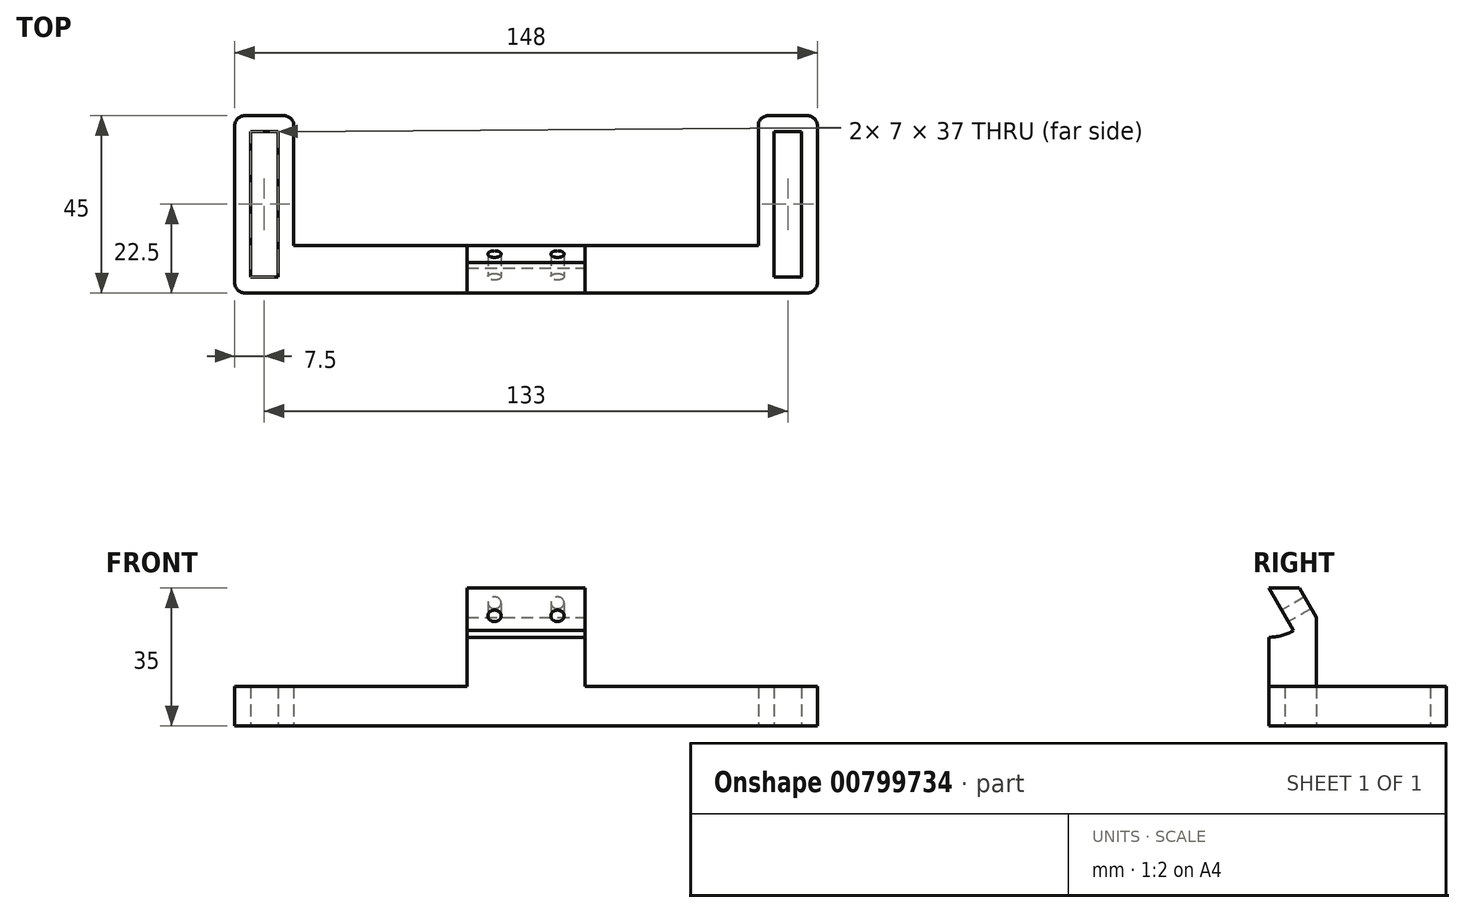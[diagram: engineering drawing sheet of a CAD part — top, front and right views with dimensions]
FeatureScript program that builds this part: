
annotation { "Feature Type Name" : "Feature", "Feature Type Description" : "" }
export const myFeature = defineFeature(function(context is Context, id is Id, definition is map)
    precondition{}
    {
        {
            var Q0;
            Q0=qCreatedBy(makeId("Top.planeOp"),FACE);
            var sketch = newSketch(context, id + "F0", { "sketchPlane" : qUnion([Q0])});
            skPoint(sketch, "E0", {"position": v(59, 0) * mm});
            skPoint(sketch, "E1", {"position": v(-59, 0) * mm});
            skLineSegment(sketch, "E2.bottom", {"start": v(-59, 0) * mm, "end": v(-74, 0) * mm});
            skLineSegment(sketch, "E2.top", {"start": v(-59, 45) * mm, "end": v(-74, 45) * mm});
            skLineSegment(sketch, "E2.left", {"start": v(-59, 0) * mm, "end": v(-59, 45) * mm});
            skLineSegment(sketch, "E2.right", {"start": v(-74, 0) * mm, "end": v(-74, 45) * mm});
            skLineSegment(sketch, "E3.bottom", {"start": v(59, 0) * mm, "end": v(74, 0) * mm});
            skLineSegment(sketch, "E3.top", {"start": v(59, 45) * mm, "end": v(74, 45) * mm});
            skLineSegment(sketch, "E3.left", {"start": v(59, 0) * mm, "end": v(59, 45) * mm});
            skLineSegment(sketch, "E3.right", {"start": v(74, 0) * mm, "end": v(74, 45) * mm});
            skPoint(sketch, "E4", {"position": v(59, 12) * mm});
            skPoint(sketch, "E5", {"position": v(-59, 12) * mm});
            skLineSegment(sketch, "E6", {"start": v(-59, 12) * mm, "end": v(59, 12) * mm});
            skLineSegment(sketch, "E7", {"start": v(-59, 0) * mm, "end": v(59, 0) * mm});
            skLineSegment(sketch, "E8.0", {"start": v(-70, 4) * mm, "end": v(-70, 41) * mm});
            skLineSegment(sketch, "E8.1", {"start": v(-63, 4) * mm, "end": v(-70, 4) * mm});
            skLineSegment(sketch, "E8.2", {"start": v(-63, 4) * mm, "end": v(-63, 41) * mm});
            skLineSegment(sketch, "E8.3", {"start": v(-63, 41) * mm, "end": v(-70, 41) * mm});
            skLineSegment(sketch, "E9.0", {"start": v(70, 4) * mm, "end": v(70, 41) * mm});
            skLineSegment(sketch, "E9.1", {"start": v(63, 4) * mm, "end": v(70, 4) * mm});
            skLineSegment(sketch, "E9.2", {"start": v(63, 4) * mm, "end": v(63, 41) * mm});
            skLineSegment(sketch, "E9.3", {"start": v(63, 41) * mm, "end": v(70, 41) * mm});
            skSolve(sketch);
        }
        {
            var Q0;
            {var subQ2=sQuery(id+"F0.wireOp",EDGE,"E6");Q0=makeQuery(id+"F0.imprint","IMPRINT",FACE,{"disambiguationData":[TD([[makeQuery(id+"F0.imprint","IMPRINT",EDGE,{"derivedFrom":subQ2}),-1.0]])]});}
            var Q1;
            {var subQ1=sQuery(id+"F0.wireOp",EDGE,"E2.bottom");Q1=makeQuery(id+"F0.imprint","IMPRINT",FACE,{"disambiguationData":[TD([[makeQuery(id+"F0.imprint","IMPRINT",EDGE,{"derivedFrom":subQ1}),-1.0]])]});}
            var Q2;
            {var subQ1=sQuery(id+"F0.wireOp",EDGE,"E3.bottom");Q2=makeQuery(id+"F0.imprint","IMPRINT",FACE,{"disambiguationData":[TD([[makeQuery(id+"F0.imprint","IMPRINT",EDGE,{"derivedFrom":subQ1}),1.0]])]});}
            extrude(context, id + "F1", {"entities" : qUnion([Q0, Q1, Q2]), "depth" : 10 * mm, "offsetDistance" : 25 * mm});
        }
        {
            var Q0;
            Q0=makeQuery(id+"F1.opExtrude","CAP_FACE",FACE,{"disambiguationData":[OSD([sQuery(id+"F0.wireOp",EDGE,"E2.bottom"),sQuery(id+"F0.wireOp",EDGE,"E2.top"),sQuery(id+"F0.wireOp",EDGE,"E2.left"),sQuery(id+"F0.wireOp",EDGE,"E2.right"),sQuery(id+"F0.wireOp",EDGE,"E3.bottom"),sQuery(id+"F0.wireOp",EDGE,"E3.top"),sQuery(id+"F0.wireOp",EDGE,"E3.left"),sQuery(id+"F0.wireOp",EDGE,"E3.right"),sQuery(id+"F0.wireOp",EDGE,"E6"),sQuery(id+"F0.wireOp",EDGE,"E7"),sQuery(id+"F0.wireOp",EDGE,"E8.0"),sQuery(id+"F0.wireOp",EDGE,"E8.1"),sQuery(id+"F0.wireOp",EDGE,"E8.2"),sQuery(id+"F0.wireOp",EDGE,"E8.3"),sQuery(id+"F0.wireOp",EDGE,"E9.0"),sQuery(id+"F0.wireOp",EDGE,"E9.1"),sQuery(id+"F0.wireOp",EDGE,"E9.2"),sQuery(id+"F0.wireOp",EDGE,"E9.3")])],"isStart":false});
            var sketch = newSketch(context, id + "F2", { "sketchPlane" : qUnion([Q0])});
            skPoint(sketch, "E10", {"position": v(0, 12) * mm});
            skPoint(sketch, "E11", {"position": v(-15, 12) * mm});
            skPoint(sketch, "E12", {"position": v(15, 12) * mm});
            skPoint(sketch, "E13", {"position": v(15, 0) * mm});
            skPoint(sketch, "E14", {"position": v(-15, 0) * mm});
            skLineSegment(sketch, "E15", {"start": v(-15, 12) * mm, "end": v(-15, 0) * mm});
            skLineSegment(sketch, "E16", {"start": v(15, 12) * mm, "end": v(15, 0) * mm});
            skSolve(sketch);
        }
        {
            var Q0;
            {var subQ0=sQuery(id+"F2.wireOp",EDGE,"E15");Q0=makeQuery(id+"F2.imprint","IMPRINT",FACE,{"disambiguationData":[TD([[makeQuery(id+"F2.imprint","IMPRINT",EDGE,{"derivedFrom":subQ0}),1.0]])]});}
            extrude(context, id + "F3", {"entities" : qUnion([Q0]), "operationType" : NewBodyOperationType.ADD, "depth" : 25 * mm, "offsetDistance" : 25 * mm});
        }
        {
            var Q0;
            Q0=makeQuery(id+"F3.opExtrude","CAP_EDGE",EDGE,{"disambiguationData":[OSD([sQuery(id+"F0.wireOp",EDGE,"E6")])],"isStart":false});
            chamfer(context, id + "F4", {"entities" : qUnion([Q0]), "chamferType" : ChamferType.OFFSET_ANGLE, "width" : 7.5 * mm, "oppositeDirection" : false, "angle" : 30 * degree, "tangentPropagation" : true});
        }
        {
            var Q0;
            Q0=makeQuery(id+"F4.opChamfer","BLEND_FACE",FACE,{"disambiguationData":[OSD([sQuery(id+"F0.wireOp",EDGE,"E6")])]});
            var sketch = newSketch(context, id + "F5", { "sketchPlane" : qUnion([Q0])});
            skPoint(sketch, "E17", {"position": v(8, 22.15) * mm});
            skPoint(sketch, "E17.positionSnap0", {"position": v(15, 22.15) * mm});
            skPoint(sketch, "E18", {"position": v(-8, 22.15) * mm});
            skSolve(sketch);
        }
        {
            var Q0;
            {var subQ0=sQuery(id+"F0.wireOp",EDGE,"E7");var subQ1=sQuery(id+"F0.wireOp",EDGE,"E3.bottom");var subQ2=sQuery(id+"F0.wireOp",EDGE,"E2.bottom");Q0=makeQuery(id+"F3.boolean.opBoolean","MERGE",FACE,{"derivedFrom":[makeQuery(id+"F1.opExtrude","SWEPT_FACE",FACE,{"disambiguationData":[OSD([subQ2,subQ1,subQ0])]}),makeQuery(id+"F3.opExtrude","SWEPT_FACE",FACE,{"disambiguationData":[OSD([subQ2,subQ1,subQ0])]})]});}
            var sketch = newSketch(context, id + "F6", { "sketchPlane" : qUnion([Q0])});
            skPoint(sketch, "E19", {"position": v(-15, 22.5) * mm});
            skPoint(sketch, "E20", {"position": v(15, 22.5) * mm});
            skLineSegment(sketch, "E21", {"start": v(-15, 22.5) * mm, "end": v(15, 22.5) * mm});
            skSolve(sketch);
        }
        {
            var Q0;
            {var subQ5=sQuery(id+"F6.wireOp",EDGE,"E21");Q0=makeQuery(id+"F6.imprint","IMPRINT",FACE,{"disambiguationData":[TD([[makeQuery(id+"F6.imprint","IMPRINT",EDGE,{"derivedFrom":subQ5}),1.0]])]});}
            var Q1;
            Q1=makeQuery(id+"F3.opExtrude","CAP_EDGE",EDGE,{"disambiguationData":[OSD([sQuery(id+"F0.wireOp",EDGE,"E2.bottom"),sQuery(id+"F0.wireOp",EDGE,"E3.bottom"),sQuery(id+"F0.wireOp",EDGE,"E7")])],"isStart":false});
            revolve(context, id + "F7", {"operationType" : NewBodyOperationType.REMOVE, "surfaceOperationType" : NewSurfaceOperationType.NEW, "entities" : qUnion([Q0]), "axis" : qUnion([Q1]), "revolveType" : RevolveType.ONE_DIRECTION, "angle" : 30 * degree});
        }
        {
            var Q0;
            Q0=sQuery(id+"F5.wireOp",VERTEX,"E17");
            var Q1;
            Q1=sQuery(id+"F5.wireOp",VERTEX,"E18");
            var Q2;
            Q2=makeQuery(id+"F1.opExtrude","SWEPT_BODY",BODY,{"disambiguationData":[OSD([sQuery(id+"F0.wireOp",EDGE,"E2.bottom"),sQuery(id+"F0.wireOp",EDGE,"E2.top"),sQuery(id+"F0.wireOp",EDGE,"E2.left"),sQuery(id+"F0.wireOp",EDGE,"E2.right"),sQuery(id+"F0.wireOp",EDGE,"E3.bottom"),sQuery(id+"F0.wireOp",EDGE,"E3.top"),sQuery(id+"F0.wireOp",EDGE,"E3.left"),sQuery(id+"F0.wireOp",EDGE,"E3.right"),sQuery(id+"F0.wireOp",EDGE,"E6"),sQuery(id+"F0.wireOp",EDGE,"E7"),sQuery(id+"F0.wireOp",EDGE,"E8.0"),sQuery(id+"F0.wireOp",EDGE,"E8.1"),sQuery(id+"F0.wireOp",EDGE,"E8.2"),sQuery(id+"F0.wireOp",EDGE,"E8.3"),sQuery(id+"F0.wireOp",EDGE,"E9.0"),sQuery(id+"F0.wireOp",EDGE,"E9.1"),sQuery(id+"F0.wireOp",EDGE,"E9.2"),sQuery(id+"F0.wireOp",EDGE,"E9.3")])]});
            hole(context, id + "F8", {"style" : HoleStyle.SIMPLE, "endStyle" : HoleEndStyle.THROUGH, "standardTappedOrClearance" : lookupTablePath({ "fit" : "Normal", "standard" : "ISO", "size" : "M3", "type" : "Clearance" }), "standardBlindInLast" : lookupTablePath({ "fit" : "Normal", "standard" : "ISO", "engagement" : "75%", "pitch" : "0.5 mm", "size" : "M3", "type" : "Clearance & tapped" }), "holeDiameter" : 3.4 * mm, "majorDiameter" : 5 * mm, "isTappedThrough" : true, "tappedDepth" : 12 * mm, "tapClearance" : 3, "startFromSketch" : true, "locations" : qUnion([Q0, Q1]), "scope" : qUnion([Q2])});
        }
        {
            var Q0;
            Q0=makeQuery(id+"F1.opExtrude","SWEPT_EDGE",EDGE,{"disambiguationData":[OSD([sQuery(id+"F0.wireOp",EDGE,"E2.bottom"),sQuery(id+"F0.wireOp",EDGE,"E2.right")])]});
            var Q1;
            Q1=makeQuery(id+"F3.opExtrude","CAP_EDGE",EDGE,{"disambiguationData":[OSD([sQuery(id+"F2.wireOp",EDGE,"E15")])],"isStart":true});
            var Q2;
            Q2=makeQuery(id+"F3.opExtrude","CAP_EDGE",EDGE,{"disambiguationData":[OSD([sQuery(id+"F2.wireOp",EDGE,"E16")])],"isStart":true});
            var Q3;
            Q3=makeQuery(id+"F1.opExtrude","SWEPT_EDGE",EDGE,{"disambiguationData":[OSD([sQuery(id+"F0.wireOp",EDGE,"E3.bottom"),sQuery(id+"F0.wireOp",EDGE,"E3.right")])]});
            var Q4;
            Q4=makeQuery(id+"F1.opExtrude","SWEPT_EDGE",EDGE,{"disambiguationData":[OSD([sQuery(id+"F0.wireOp",EDGE,"E3.top"),sQuery(id+"F0.wireOp",EDGE,"E3.right")])]});
            var Q5;
            Q5=makeQuery(id+"F1.opExtrude","SWEPT_EDGE",EDGE,{"disambiguationData":[OSD([sQuery(id+"F0.wireOp",EDGE,"E3.top"),sQuery(id+"F0.wireOp",EDGE,"E3.left")])]});
            var Q6;
            Q6=makeQuery(id+"F1.opExtrude","SWEPT_EDGE",EDGE,{"disambiguationData":[OSD([sQuery(id+"F0.wireOp",EDGE,"E2.top"),sQuery(id+"F0.wireOp",EDGE,"E2.right")])]});
            var Q7;
            Q7=makeQuery(id+"F1.opExtrude","SWEPT_EDGE",EDGE,{"disambiguationData":[OSD([sQuery(id+"F0.wireOp",EDGE,"E2.top"),sQuery(id+"F0.wireOp",EDGE,"E2.left")])]});
            fillet(context, id + "F9", {"entities" : qUnion([Q0, Q1, Q2, Q3, Q4, Q5, Q6, Q7]), "tangentPropagation" : true, "radius" : 2.5 * mm, "defaultsChanged" : false, "vertexSettings" : [], "allowEdgeOverflow" : false});
        }
    });
